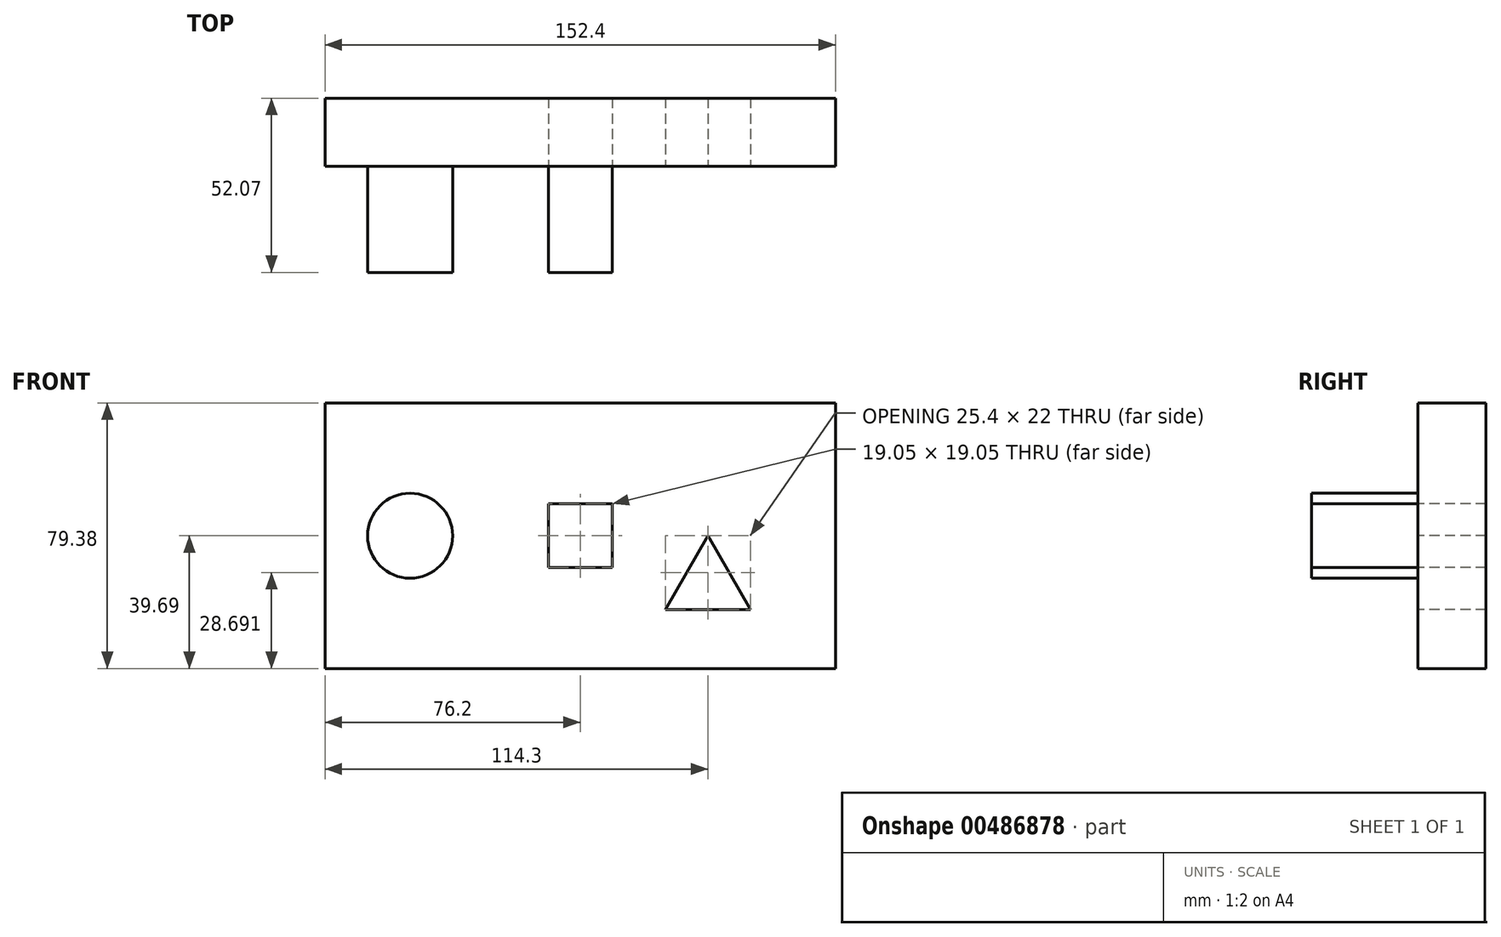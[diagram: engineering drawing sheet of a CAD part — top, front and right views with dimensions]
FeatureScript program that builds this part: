
annotation { "Feature Type Name" : "Feature", "Feature Type Description" : "" }
export const myFeature = defineFeature(function(context is Context, id is Id, definition is map)
    precondition{}
    {
        {
            var Q0;
            Q0=qCreatedBy(makeId("Front.planeOp"),FACE);
            var sketch = newSketch(context, id + "F0", { "sketchPlane" : qUnion([Q0])});
            skLineSegment(sketch, "E0", {"start": v(6.35, 0) * mm, "end": v(-6.35, -22) * mm});
            skLineSegment(sketch, "E1", {"start": v(-6.35, -22) * mm, "end": v(19.05, -22) * mm});
            skLineSegment(sketch, "E2", {"start": v(19.05, -22) * mm, "end": v(6.35, 0) * mm});
            skLineSegment(sketch, "E3.bottom", {"start": v(-22.22, 9.52) * mm, "end": v(-41.27, 9.53) * mm});
            skLineSegment(sketch, "E3.top", {"start": v(-22.23, -9.53) * mm, "end": v(-41.27, -9.52) * mm});
            skLineSegment(sketch, "E3.left", {"start": v(-22.22, 9.52) * mm, "end": v(-22.23, -9.53) * mm});
            skLineSegment(sketch, "E3.right", {"start": v(-41.27, 9.53) * mm, "end": v(-41.27, -9.52) * mm});
            skPoint(sketch, "E3.middle", {"position": v(-31.75, 0) * mm});
            skCircle(sketch, "E4", {"center": v(-82.55, 0) * mm, "radius": 12.7 * mm});
            skPoint(sketch, "E5.middle", {"position": v(0, 0) * mm});
            skLineSegment(sketch, "E6", {"start": v(0, 0) * mm, "end": v(44.45, 0) * mm});
            skLineSegment(sketch, "E7.bottom", {"start": v(44.45, -39.69) * mm, "end": v(-107.95, -39.69) * mm});
            skLineSegment(sketch, "E7.top", {"start": v(44.45, 39.69) * mm, "end": v(-107.95, 39.69) * mm});
            skLineSegment(sketch, "E7.left", {"start": v(44.45, -39.69) * mm, "end": v(44.45, 39.69) * mm});
            skLineSegment(sketch, "E7.right", {"start": v(-107.95, -39.69) * mm, "end": v(-107.95, 39.69) * mm});
            skSolve(sketch);
        }
        {
            var Q0;
            Q0 = qSketchRegion(id + "F0", true);
            var Q1;
            Q1=makeQuery(id+"F0.imprint","IMPRINT",FACE,{"disambiguationData":[TD([[makeQuery(id+"F0.imprint","IMPRINT",EDGE,{"derivedFrom":sQuery(id+"F0.wireOp",EDGE,"E4")}),1.0]])]});
            extrude(context, id + "F1", {"entities" : qUnion([Q0, Q1]), "oppositeDirection" : true, "depth" : 20.32 * mm});
        }
        {
            var Q0;
            Q0=makeQuery(id+"F0.imprint","IMPRINT",FACE,{"disambiguationData":[TD([[makeQuery(id+"F0.imprint","IMPRINT",EDGE,{"derivedFrom":sQuery(id+"F0.wireOp",EDGE,"E4")}),1.0]])]});
            var Q1;
            Q1=makeQuery(id+"F0.imprint","IMPRINT",FACE,{"disambiguationData":[TD([[makeQuery(id+"F0.imprint","IMPRINT",EDGE,{"derivedFrom":sQuery(id+"F0.wireOp",EDGE,"E3.bottom")}),1.0]])]});
            extrude(context, id + "F2", {"entities" : qUnion([Q0, Q1]), "depth" : 31.75 * mm});
        }
    });
